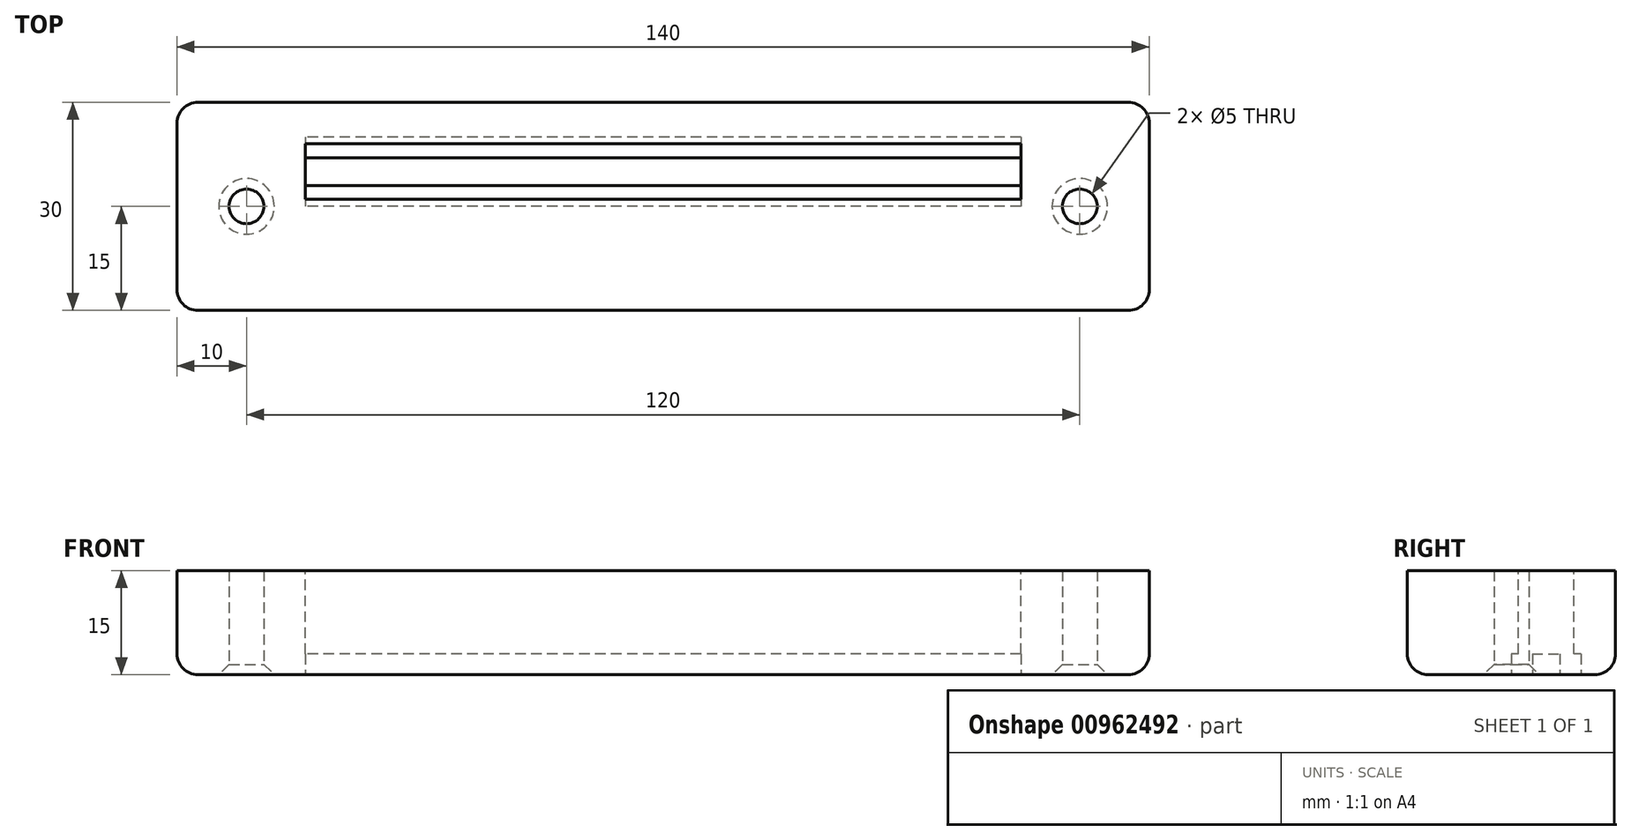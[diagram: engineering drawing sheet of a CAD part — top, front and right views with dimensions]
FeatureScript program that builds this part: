
annotation { "Feature Type Name" : "Feature", "Feature Type Description" : "" }
export const myFeature = defineFeature(function(context is Context, id is Id, definition is map)
    precondition{}
    {
        {
            var Q0;
            Q0=qCreatedBy(makeId("Top.planeOp"),FACE);
            var sketch = newSketch(context, id + "F0", { "sketchPlane" : qUnion([Q0])});
            skLineSegment(sketch, "E0.bottom", {"start": v(67, -20) * mm, "end": v(-67, -20) * mm});
            skLineSegment(sketch, "E0.top", {"start": v(67, 10) * mm, "end": v(-67, 10) * mm});
            skLineSegment(sketch, "E0.left", {"start": v(70, -17) * mm, "end": v(70, 7) * mm});
            skLineSegment(sketch, "E0.right", {"start": v(-70, -17) * mm, "end": v(-70, 7) * mm});
            skPoint(sketch, "E0.middle", {"position": v(0, 0) * mm});
            skPoint(sketch, "E1.visualSharp", {"position": v(70, 10) * mm});
            skArc(sketch, "E1.filletArc", {"start": v(70, 7) * mm, "mid": v(69.12, 9.12) * mm, "end": v(67, 10) * mm});
            skPoint(sketch, "E2.visualSharp", {"position": v(70, -10) * mm});
            skArc(sketch, "E2.filletArc", {"start": v(67, -20) * mm, "mid": v(69.12, -19.12) * mm, "end": v(70, -17) * mm});
            skPoint(sketch, "E3.visualSharp", {"position": v(-70, 10) * mm});
            skArc(sketch, "E3.filletArc", {"start": v(-67, 10) * mm, "mid": v(-69.12, 9.12) * mm, "end": v(-70, 7) * mm});
            skPoint(sketch, "E4.visualSharp", {"position": v(-70, -10) * mm});
            skArc(sketch, "E4.filletArc", {"start": v(-70, -17) * mm, "mid": v(-69.12, -19.12) * mm, "end": v(-67, -20) * mm});
            skSolve(sketch);
        }
        {
            var Q0;
            Q0=makeQuery(id+"F0.imprint","IMPRINT",FACE,{"disambiguationData":[TD([[makeQuery(id+"F0.imprint","IMPRINT",EDGE,{"derivedFrom":sQuery(id+"F0.wireOp",EDGE,"E0.bottom")}),-1.0]])]});
            extrude(context, id + "F1", {"entities" : qUnion([Q0]), "depth" : 15 * mm, "offsetDistance" : 25 * mm});
        }
        {
            var Q0;
            Q0=makeQuery(id+"F1.opExtrude","CAP_FACE",FACE,{"disambiguationData":[OSD([sQuery(id+"F0.wireOp",EDGE,"E0.bottom"),sQuery(id+"F0.wireOp",EDGE,"E0.top"),sQuery(id+"F0.wireOp",EDGE,"E0.left"),sQuery(id+"F0.wireOp",EDGE,"E0.right"),sQuery(id+"F0.wireOp",EDGE,"E1.filletArc"),sQuery(id+"F0.wireOp",EDGE,"E2.filletArc"),sQuery(id+"F0.wireOp",EDGE,"E3.filletArc"),sQuery(id+"F0.wireOp",EDGE,"E4.filletArc")])],"isStart":true});
            fillet(context, id + "F2", {"entities" : qUnion([Q0]), "radius" : 3 * mm, "tangentPropagation" : true, "allowEdgeOverflow" : false});
        }
        {
            var Q0;
            Q0=makeQuery(id+"F1.opExtrude","CAP_FACE",FACE,{"disambiguationData":[OSD([sQuery(id+"F0.wireOp",EDGE,"E0.bottom"),sQuery(id+"F0.wireOp",EDGE,"E0.top"),sQuery(id+"F0.wireOp",EDGE,"E0.left"),sQuery(id+"F0.wireOp",EDGE,"E0.right"),sQuery(id+"F0.wireOp",EDGE,"25XE0SJy-i2tU-syPD-Ji9C-Y5MA9KGGyTkM.bottom"),sQuery(id+"F0.wireOp",EDGE,"25XE0SJy-i2tU-syPD-Ji9C-Y5MA9KGGyTkM.top"),sQuery(id+"F0.wireOp",EDGE,"25XE0SJy-i2tU-syPD-Ji9C-Y5MA9KGGyTkM.left"),sQuery(id+"F0.wireOp",EDGE,"25XE0SJy-i2tU-syPD-Ji9C-Y5MA9KGGyTkM.right")])],"isStart":false});
            var sketch = newSketch(context, id + "F3", { "sketchPlane" : qUnion([Q0])});
            skPoint(sketch, "E5.0", {"position": v(0, 0) * mm});
            skLineSegment(sketch, "E6.bottom", {"start": v(51.5, -4) * mm, "end": v(-51.5, -4) * mm});
            skLineSegment(sketch, "E6.top", {"start": v(51.5, 4) * mm, "end": v(-51.5, 4) * mm});
            skLineSegment(sketch, "E6.left", {"start": v(51.5, -4) * mm, "end": v(51.5, 4) * mm});
            skLineSegment(sketch, "E6.right", {"start": v(-51.5, -4) * mm, "end": v(-51.5, 4) * mm});
            skPoint(sketch, "E7", {"position": v(-64, 0) * mm});
            skPoint(sketch, "E8", {"position": v(64, 0) * mm});
            skSolve(sketch);
        }
        {
            var Q0;
            {var subQ0=sQuery(id+"F3.wireOp",EDGE,"E6.top");Q0=makeQuery(id+"F3.imprint","IMPRINT",FACE,{"disambiguationData":[TD([[makeQuery(id+"F3.imprint","IMPRINT",EDGE,{"derivedFrom":subQ0}),1.0]])]});}
            var Q1;
            {var subQ0=sQuery(id+"F3.wireOp",EDGE,"E6.bottom");Q1=makeQuery(id+"F3.imprint","IMPRINT",FACE,{"disambiguationData":[TD([[makeQuery(id+"F3.imprint","IMPRINT",EDGE,{"derivedFrom":subQ0}),-1.0]])]});}
            extrude(context, id + "F4", {"entities" : qUnion([Q0, Q1]), "operationType" : NewBodyOperationType.REMOVE, "oppositeDirection" : true, "depth" : 12 * mm, "offsetDistance" : 25 * mm});
        }
        {
            var Q0;
            Q0=makeQuery(id+"F1.opExtrude","CAP_FACE",FACE,{"disambiguationData":[OSD([sQuery(id+"F0.wireOp",EDGE,"E0.bottom"),sQuery(id+"F0.wireOp",EDGE,"E0.top"),sQuery(id+"F0.wireOp",EDGE,"E0.left"),sQuery(id+"F0.wireOp",EDGE,"E0.right"),sQuery(id+"F0.wireOp",EDGE,"E1.filletArc"),sQuery(id+"F0.wireOp",EDGE,"E2.filletArc"),sQuery(id+"F0.wireOp",EDGE,"E3.filletArc"),sQuery(id+"F0.wireOp",EDGE,"E4.filletArc")])],"isStart":true});
            var sketch = newSketch(context, id + "F5", { "sketchPlane" : qUnion([Q0])});
            skPoint(sketch, "E9.0", {"position": v(-51.5, 4) * mm});
            skPoint(sketch, "E9.1", {"position": v(-51.5, -4) * mm});
            skPoint(sketch, "E9.2", {"position": v(51.5, -4) * mm});
            skPoint(sketch, "E9.3", {"position": v(51.5, 4) * mm});
            skLineSegment(sketch, "E10", {"start": v(-51.5, 4) * mm, "end": v(51.5, 4) * mm, "construction": true});
            skLineSegment(sketch, "E11", {"start": v(51.5, -4) * mm, "end": v(51.5, 4) * mm, "construction": true});
            skLineSegment(sketch, "E12", {"start": v(51.5, -4) * mm, "end": v(-51.5, -4) * mm, "construction": true});
            skLineSegment(sketch, "E13", {"start": v(-51.5, -4) * mm, "end": v(-51.5, 4) * mm, "construction": true});
            skLineSegment(sketch, "E14.bottom", {"start": v(51.5, -5) * mm, "end": v(-51.5, -5) * mm});
            skLineSegment(sketch, "E14.top", {"start": v(51.5, 5) * mm, "end": v(-51.5, 5) * mm});
            skLineSegment(sketch, "E14.left", {"start": v(51.5, -5) * mm, "end": v(51.5, 5) * mm});
            skLineSegment(sketch, "E14.right", {"start": v(-51.5, -5) * mm, "end": v(-51.5, 5) * mm});
            skPoint(sketch, "E14.middle", {"position": v(0, 0) * mm});
            skLineSegment(sketch, "E15.bottom", {"start": v(51.5, -2) * mm, "end": v(-51.5, -2) * mm});
            skLineSegment(sketch, "E15.top", {"start": v(51.5, 2) * mm, "end": v(-51.5, 2) * mm});
            skLineSegment(sketch, "E15.left", {"start": v(51.5, -2) * mm, "end": v(51.5, 2) * mm});
            skLineSegment(sketch, "E15.right", {"start": v(-51.5, -2) * mm, "end": v(-51.5, 2) * mm});
            skSolve(sketch);
        }
        {
            var Q0;
            {var subQ0=sQuery(id+"F5.wireOp",EDGE,"E14.top");Q0=makeQuery(id+"F5.imprint","IMPRINT",FACE,{"disambiguationData":[TD([[makeQuery(id+"F5.imprint","IMPRINT",EDGE,{"derivedFrom":subQ0}),1.0]])]});}
            var Q1;
            {var subQ0=sQuery(id+"F5.wireOp",EDGE,"E14.bottom");Q1=makeQuery(id+"F5.imprint","IMPRINT",FACE,{"disambiguationData":[TD([[makeQuery(id+"F5.imprint","IMPRINT",EDGE,{"derivedFrom":subQ0}),-1.0]])]});}
            extrude(context, id + "F6", {"entities" : qUnion([Q0, Q1]), "operationType" : NewBodyOperationType.REMOVE, "oppositeDirection" : true, "depth" : 3 * mm, "offsetDistance" : 25 * mm});
        }
        {
            var Q0;
            Q0=makeQuery(id+"F0.imprint","IMPRINT",FACE,{"disambiguationData":[TD([[makeQuery(id+"F0.imprint","IMPRINT",EDGE,{"derivedFrom":sQuery(id+"F0.wireOp",EDGE,"E0.bottom")}),-1.0]])]});
            var sketch = newSketch(context, id + "F7", { "sketchPlane" : qUnion([Q0])});
            skPoint(sketch, "E16.0", {"position": v(70, -5) * mm});
            skPoint(sketch, "E16.1", {"position": v(-70, -5) * mm});
            skLineSegment(sketch, "E17", {"start": v(70, -5) * mm, "end": v(-70, -5) * mm, "construction": true});
            skPoint(sketch, "E18", {"position": v(60, -5) * mm});
            skPoint(sketch, "E19", {"position": v(-60, -5) * mm});
            skSolve(sketch);
        }
        {
            var Q0;
            Q0=sQuery(id+"F7.wireOp",VERTEX,"E19");
            var Q1;
            Q1=sQuery(id+"F7.wireOp",VERTEX,"E18");
            var Q2;
            Q2=makeQuery(id+"F1.opExtrude","SWEPT_BODY",BODY,{"disambiguationData":[OSD([sQuery(id+"F0.wireOp",EDGE,"E0.bottom"),sQuery(id+"F0.wireOp",EDGE,"E0.top"),sQuery(id+"F0.wireOp",EDGE,"E0.left"),sQuery(id+"F0.wireOp",EDGE,"E0.right"),sQuery(id+"F0.wireOp",EDGE,"25XE0SJy-i2tU-syPD-Ji9C-Y5MA9KGGyTkM.bottom"),sQuery(id+"F0.wireOp",EDGE,"25XE0SJy-i2tU-syPD-Ji9C-Y5MA9KGGyTkM.top"),sQuery(id+"F0.wireOp",EDGE,"25XE0SJy-i2tU-syPD-Ji9C-Y5MA9KGGyTkM.left"),sQuery(id+"F0.wireOp",EDGE,"25XE0SJy-i2tU-syPD-Ji9C-Y5MA9KGGyTkM.right")])]});
            hole(context, id + "F8", {"style" : HoleStyle.C_SINK, "endStyle" : HoleEndStyle.THROUGH, "oppositeDirection" : true, "holeDiameter" : 5 * mm, "cSinkDiameter" : 8 * mm, "cSinkAngle" : 90 * degree, "majorDiameter" : 5 * mm, "isTappedThrough" : true, "tappedDepth" : 12 * mm, "tapClearance" : 3, "locations" : qUnion([Q0, Q1]), "scope" : qUnion([Q2])});
        }
    });
